# Revit family: Valve
name_source: partatom
category: Pipe Accessories
revit_build: Autodesk Revit 2014 (Build: 20130709_2115(x64)
units: mm (PartAtom-declared; Revit-internal decimal feet)

## types (5) — shared parameters
Air Port Diameter = 0' - 0 1/2"
Air Port Separation = 0' - 0 3/4"

## per-type parameters (varying)
| type | Actuator Base | Actuator Base Offset | Actuator Base Side | Actuator Base to CL | Actuator Square Elevation | Actuator Square Length | Actuator Square Size | Air Port Height | Air Port Length | Clamp Face to Hub | D3 | Extrusion Edge Length | Extrusion Height | Extrusion Length | H3 | Horizontal Center | Hub Radius | L | Pipe Diameter | Pipe Radius | R3 |
| .5" | 0' - 1 11/16" | 0' - 1 9/32" | 0' - 0 27/32" | 0' - 0 5/16" | 0' - 3 23/32" | 0' - 1 11/16" | 0' - 0 5/8" | 0' - 2 23/32" | 0' - 1 13/16" | 0' - 1 1/16" | 0' - 3 5/32" | 0' - 0 3/4" | 0' - 4 1/16" | 0' - 1 9/16" | 0' - 5 7/16" | 0' - 2 1/8" | 0' - 0 3/8" | 0' - 4 1/4" | 0' - 0 1/2" | 0' - 0 1/4" | 0' - 1 9/16" |
| .75" | 0' - 1 27/32" | 0' - 1 3/8" | 0' - 0 15/16" | 0' - 0 15/32" | 0' - 5 1/16" | 0' - 2 1/8" | 0' - 0 25/32" | 0' - 3 7/16" | 0' - 2 1/4" | 0' - 1 5/32" | 0' - 3 31/32" | 0' - 1 1/8" | 0' - 5 1/8" | 0' - 2" | 0' - 6 27/32" | 0' - 2 5/16" | 0' - 0 9/16" | 0' - 4 5/8" | 0' - 0 3/4" | 0' - 0 3/8" | 0' - 2" |
| 1" | 0' - 2" | 0' - 1 1/2" | 0' - 1" | 0' - 0 5/8" | 0' - 5 3/16" | 0' - 2 1/8" | 0' - 0 25/32" | 0' - 3 1/2" | 0' - 2 1/4" | 0' - 1 1/4" | 0' - 3 31/32" | 0' - 1 1/2" | 0' - 5 7/32" | 0' - 2" | 0' - 6 31/32" | 0' - 2 1/2" | 0' - 0 3/4" | 0' - 5" | 0' - 1" | 0' - 0 1/2" | 0' - 2" |
| 1.5" | 0' - 2 1/2" | 0' - 1 7/8" | 0' - 1 1/4" | 0' - 0 15/16" | 0' - 8 25/32" | 0' - 3 1/8" | 0' - 1 3/16" | 0' - 5 11/32" | 0' - 3 1/4" | 0' - 1 9/16" | 0' - 6 1/32" | 0' - 2 1/4" | 0' - 8 1/32" | 0' - 3" | 0' - 10 23/32" | 0' - 3 1/8" | 0' - 1 1/8" | 0' - 6 1/4" | 0' - 1 1/2" | 0' - 0 3/4" | 0' - 3" |
| 2" | 0' - 3" | 0' - 2 1/4" | 0' - 1 1/2" | 0' - 1 1/4" | 0' - 9" | 0' - 3 1/8" | 0' - 1 3/16" | 0' - 5 15/32" | 0' - 3 1/4" | 0' - 1 7/8" | 0' - 6 1/32" | 0' - 3" | 0' - 8 7/32" | 0' - 3" | 0' - 10 15/16" | 0' - 3 3/4" | 0' - 1 1/2" | 0' - 7 15/32" | 0' - 2" | 0' - 1" | 0' - 3" |

## geometry (parser evidence)
native form markers: Extrusion x17, Sweep x19
no freeform markers — native parametric forms only
